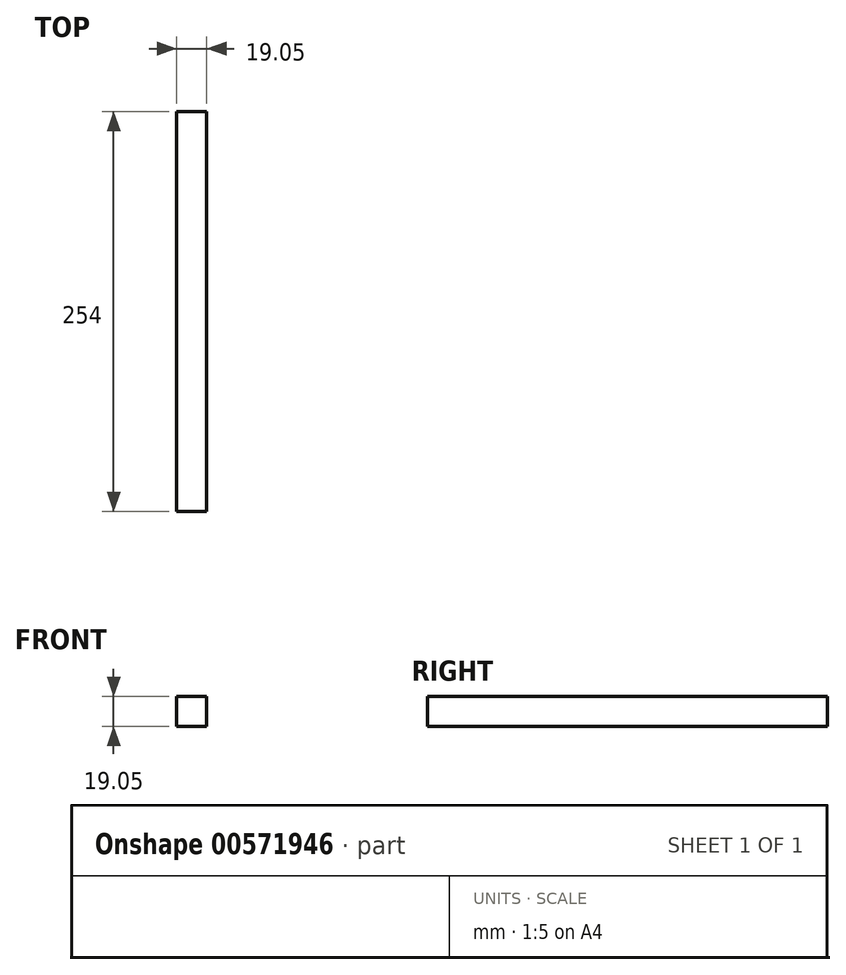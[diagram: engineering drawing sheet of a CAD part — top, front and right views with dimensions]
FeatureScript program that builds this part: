
annotation { "Feature Type Name" : "Feature", "Feature Type Description" : "" }
export const myFeature = defineFeature(function(context is Context, id is Id, definition is map)
    precondition{}
    {
        {
            var Q0;
            Q0=qCreatedBy(makeId("Top.planeOp"),FACE);
            var sketch = newSketch(context, id + "F0", { "sketchPlane" : qUnion([Q0])});
            skLineSegment(sketch, "E0.bottom", {"start": v(0, 0) * mm, "end": v(-19.05, 0) * mm});
            skLineSegment(sketch, "E0.top", {"start": v(0, -254) * mm, "end": v(-19.05, -254) * mm});
            skLineSegment(sketch, "E0.left", {"start": v(0, 0) * mm, "end": v(0, -254) * mm});
            skLineSegment(sketch, "E0.right", {"start": v(-19.05, 0) * mm, "end": v(-19.05, -254) * mm});
            skSolve(sketch);
        }
        {
            var Q0;
            Q0 = qSketchRegion(id + "F0", true);
            extrude(context, id + "F1", {"entities" : qUnion([Q0]), "depth" : 19.05 * mm, "offsetDistance" : 25.4 * mm});
        }
    });
